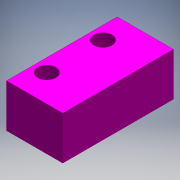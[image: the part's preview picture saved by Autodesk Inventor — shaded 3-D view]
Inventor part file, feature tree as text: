
AUTODESK INVENTOR PART (.ipt)
format: ipt  version: 2016 (Build 200138000, 138)  size: 92,672 bytes
history: native  units: mm
features: other x1, extrude x1, hole x1, sketch x1
ambient origin geometry x8: Origin, YZ Plane, XZ Plane, XY Plane, X Axis, Y Axis, Z Axis, Center Point
bodies: Solid1 (feature_tree)
feature tree (4):
  other  "Endstop.ipt"
  extrude  "Extrusion1"  Depth=5.0mm TaperAngle=0.0deg
  hole  "Hole1"  [1 undecoded]
  sketch  "Sketch1"  dims[d0=10.0mm d1=5.0mm d2=0.0mm d3=2.1mm d4=6.0mm d5=4.0mm d6=2.0mm d7=90.0deg d8=8.0mm d9=20.594885mm]
note: 1 required parameter value undecoded (feature->parameter linkage not recoverable at this tier; creation-order binding heuristic only, values carry confidence <= 0.55)
